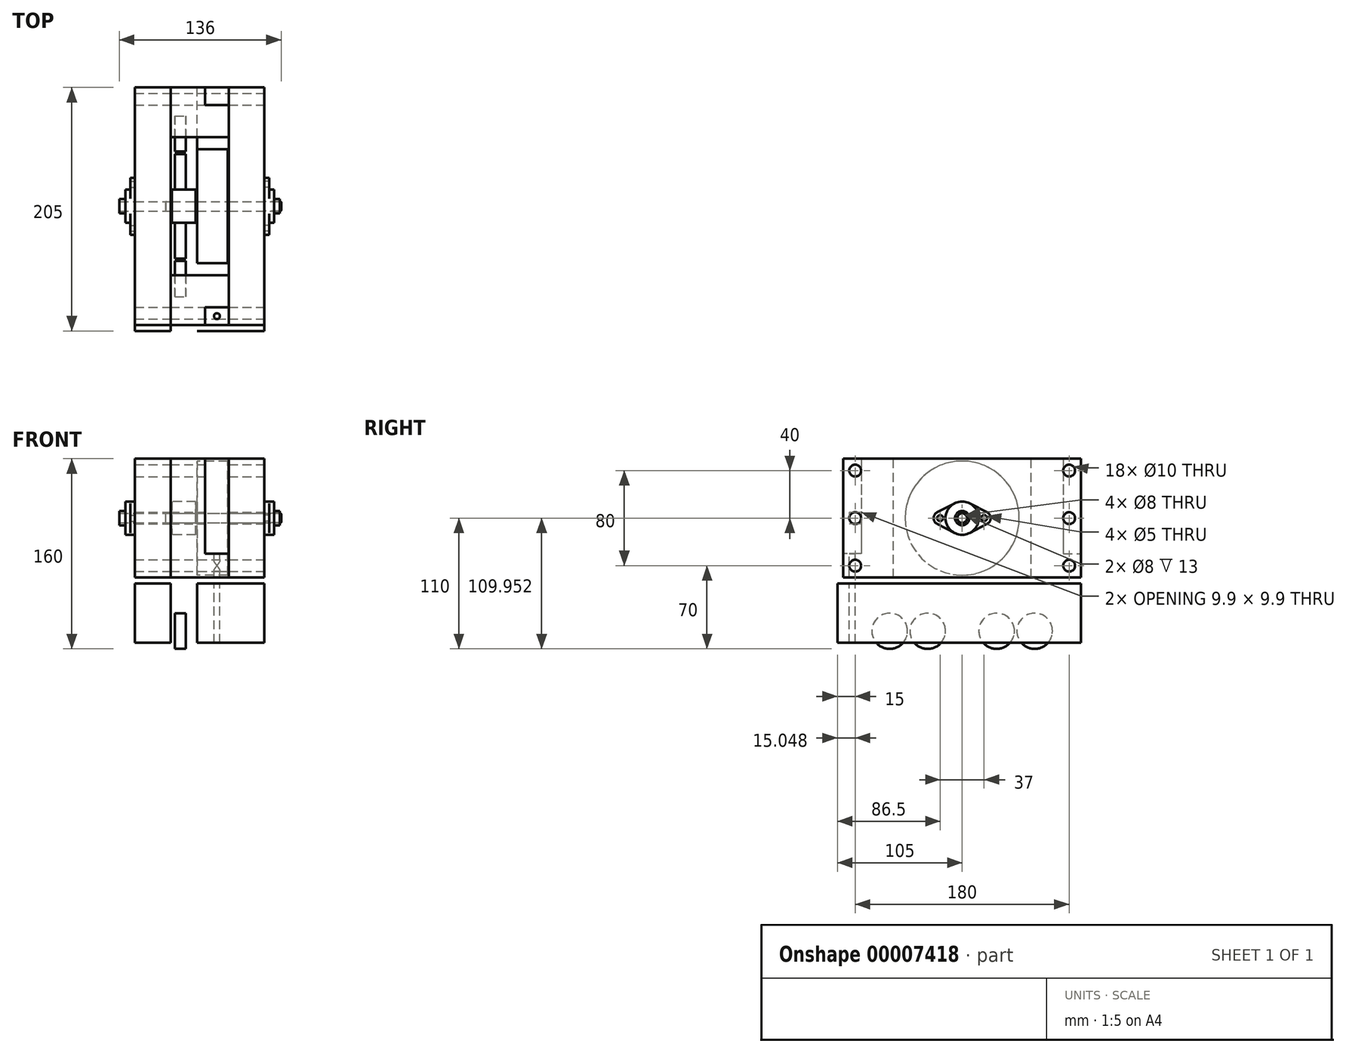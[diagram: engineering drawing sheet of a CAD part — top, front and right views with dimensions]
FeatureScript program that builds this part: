
annotation { "Feature Type Name" : "Feature", "Feature Type Description" : "" }
export const myFeature = defineFeature(function(context is Context, id is Id, definition is map)
    precondition{}
    {
        {
            var Q0;
            Q0=qCreatedBy(makeId("Front.planeOp"),FACE);
            var sketch = newSketch(context, id + "F0", { "sketchPlane" : qUnion([Q0])});
            skLineSegment(sketch, "E0.bottom", {"start": v(10, 14) * mm, "end": v(-10, 14) * mm});
            skLineSegment(sketch, "E0.top", {"start": v(10, -14) * mm, "end": v(4.5, -14) * mm});
            skLineSegment(sketch, "E0.left", {"start": v(10, 14) * mm, "end": v(10, -14) * mm});
            skLineSegment(sketch, "E0.right", {"start": v(-10, 14) * mm, "end": v(-10, -14) * mm});
            skPoint(sketch, "E0.middle", {"position": v(0, 0) * mm});
            skLineSegment(sketch, "E1", {"start": v(0, 0) * mm, "end": v(134.05, 0) * mm, "construction": true});
            skLineSegment(sketch, "E2", {"start": v(0, 0) * mm, "end": v(-79.2, 0) * mm, "construction": true});
            skLineSegment(sketch, "E3.bottom", {"start": v(-41, 15) * mm, "end": v(-56, 15) * mm});
            skLineSegment(sketch, "E3.top", {"start": v(-41, -15) * mm, "end": v(-56, -15) * mm});
            skLineSegment(sketch, "E3.left", {"start": v(-41, 15) * mm, "end": v(-41, -15) * mm});
            skLineSegment(sketch, "E3.right", {"start": v(-56, 15) * mm, "end": v(-56, -15) * mm});
            skPoint(sketch, "E3.middle", {"position": v(-48.5, 0) * mm});
            skLineSegment(sketch, "E4.bottom", {"start": v(37, 48) * mm, "end": v(21.5, 48) * mm});
            skLineSegment(sketch, "E4.top", {"start": v(37, -48) * mm, "end": v(11.5, -48) * mm});
            skLineSegment(sketch, "E4.left", {"start": v(37, 48) * mm, "end": v(37, -48) * mm});
            skLineSegment(sketch, "E4.right", {"start": v(11.5, 48) * mm, "end": v(11.5, -48) * mm});
            skPoint(sketch, "E4.middle", {"position": v(24.25, 0) * mm});
            skLineSegment(sketch, "E5.bottom", {"start": v(83, 15) * mm, "end": v(68, 15) * mm});
            skLineSegment(sketch, "E5.top", {"start": v(83, -15) * mm, "end": v(68, -15) * mm});
            skLineSegment(sketch, "E5.left", {"start": v(83, 15) * mm, "end": v(83, -15) * mm});
            skLineSegment(sketch, "E5.right", {"start": v(68, 15) * mm, "end": v(68, -15) * mm});
            skPoint(sketch, "E5.middle", {"position": v(75.5, 0) * mm});
            skLineSegment(sketch, "E6.bottom", {"start": v(13, 127.89) * mm, "end": v(43, 127.89) * mm});
            skLineSegment(sketch, "E6.top", {"start": v(13, 77.89) * mm, "end": v(43, 77.89) * mm});
            skLineSegment(sketch, "E6.left", {"start": v(13, 127.89) * mm, "end": v(13, 77.89) * mm});
            skLineSegment(sketch, "E6.right", {"start": v(43, 127.89) * mm, "end": v(43, 77.89) * mm});
            skLineSegment(sketch, "E7", {"start": v(43, 77.89) * mm, "end": v(53, 77.89) * mm});
            skLineSegment(sketch, "E8", {"start": v(53, 77.89) * mm, "end": v(53, 127.89) * mm});
            skLineSegment(sketch, "E9", {"start": v(53, 127.89) * mm, "end": v(43, 127.89) * mm});
            skLineSegment(sketch, "E10.bottom", {"start": v(68, 50) * mm, "end": v(38, 50) * mm});
            skLineSegment(sketch, "E10.top", {"start": v(68, -50) * mm, "end": v(38, -50) * mm});
            skLineSegment(sketch, "E10.left", {"start": v(68, 50) * mm, "end": v(68, -50) * mm});
            skLineSegment(sketch, "E10.right", {"start": v(38, 50) * mm, "end": v(38, -50) * mm});
            skPoint(sketch, "E10.middle", {"position": v(53, 0) * mm});
            skLineSegment(sketch, "E11.bottom", {"start": v(-11, 50) * mm, "end": v(-41, 50) * mm});
            skLineSegment(sketch, "E11.top", {"start": v(-11, -50) * mm, "end": v(-41, -50) * mm});
            skLineSegment(sketch, "E11.left", {"start": v(-11, 50) * mm, "end": v(-11, -50) * mm});
            skLineSegment(sketch, "E11.right", {"start": v(-41, 50) * mm, "end": v(-41, -50) * mm});
            skPoint(sketch, "E11.middle", {"position": v(-26, 0) * mm});
            skLineSegment(sketch, "E12.bottom", {"start": v(98, 150) * mm, "end": v(68, 150) * mm});
            skLineSegment(sketch, "E12.top", {"start": v(98, -150) * mm, "end": v(68, -150) * mm});
            skLineSegment(sketch, "E12.left", {"start": v(98, 150) * mm, "end": v(98, -150) * mm});
            skLineSegment(sketch, "E12.right", {"start": v(68, 150) * mm, "end": v(68, -150) * mm});
            skPoint(sketch, "E12.middle", {"position": v(83, 0) * mm});
            skLineSegment(sketch, "E13", {"start": v(53, 127.89) * mm, "end": v(68, 127.89) * mm, "construction": true});
            skLineSegment(sketch, "E14", {"start": v(53, 77.89) * mm, "end": v(68, 77.89) * mm, "construction": true});
            skLineSegment(sketch, "E15", {"start": v(21.5, 48) * mm, "end": v(21.5, -48) * mm, "construction": true});
            skLineSegment(sketch, "E16", {"start": v(21.5, 48) * mm, "end": v(11.5, 48) * mm});
            skLineSegment(sketch, "E17", {"start": v(48, 77.89) * mm, "end": v(48, 48) * mm, "construction": true});
            skPoint(sketch, "E18", {"position": v(29.25, 48) * mm});
            skLineSegment(sketch, "E19", {"start": v(37, 48) * mm, "end": v(37, 127.89) * mm, "construction": true});
            skLineSegment(sketch, "E20", {"start": v(43, 77.89) * mm, "end": v(43, 48) * mm, "construction": true});
            skLineSegment(sketch, "E21", {"start": v(53, 77.89) * mm, "end": v(53, 48) * mm, "construction": true});
            skCircle(sketch, "E22", {"center": v(35, 102.89) * mm, "radius": 8 * mm, "construction": true});
            skLineSegment(sketch, "E23", {"start": v(35, 102.89) * mm, "end": v(53, 102.89) * mm, "construction": true});
            skLineSegment(sketch, "E24.bottom", {"start": v(98, 127.89) * mm, "end": v(138, 127.89) * mm});
            skLineSegment(sketch, "E24.top", {"start": v(98, 77.89) * mm, "end": v(138, 77.89) * mm});
            skLineSegment(sketch, "E24.left", {"start": v(98, 127.89) * mm, "end": v(98, 77.89) * mm});
            skLineSegment(sketch, "E24.right", {"start": v(138, 127.89) * mm, "end": v(138, 77.89) * mm});
            skCircle(sketch, "E25", {"center": v(116, 102.89) * mm, "radius": 8 * mm, "construction": true});
            skLineSegment(sketch, "E26", {"start": v(116, 102.89) * mm, "end": v(98, 102.89) * mm, "construction": true});
            skLineSegment(sketch, "E27.bottom", {"start": v(-41, -55) * mm, "end": v(-11, -55) * mm});
            skLineSegment(sketch, "E27.top", {"start": v(-41, -105) * mm, "end": v(-11, -105) * mm});
            skLineSegment(sketch, "E27.left", {"start": v(-41, -55) * mm, "end": v(-41, -105) * mm});
            skLineSegment(sketch, "E27.right", {"start": v(-11, -55) * mm, "end": v(-11, -105) * mm});
            skLineSegment(sketch, "E28.bottom", {"start": v(11.5, -55) * mm, "end": v(68, -55) * mm});
            skLineSegment(sketch, "E28.top", {"start": v(11.5, -105) * mm, "end": v(68, -105) * mm});
            skLineSegment(sketch, "E28.left", {"start": v(11.5, -55) * mm, "end": v(11.5, -105) * mm});
            skLineSegment(sketch, "E28.right", {"start": v(68, -55) * mm, "end": v(68, -105) * mm});
            skLineSegment(sketch, "E29.bottom", {"start": v(1.75, -80) * mm, "end": v(-7.25, -80) * mm});
            skLineSegment(sketch, "E29.top", {"start": v(1.75, -110) * mm, "end": v(-7.25, -110) * mm});
            skLineSegment(sketch, "E29.left", {"start": v(1.75, -80) * mm, "end": v(1.75, -110) * mm});
            skLineSegment(sketch, "E29.right", {"start": v(-7.25, -80) * mm, "end": v(-7.25, -110) * mm});
            skPoint(sketch, "E29.middle", {"position": v(-2.75, -95) * mm});
            skLineSegment(sketch, "E30", {"start": v(4.5, 14) * mm, "end": v(4.5, -14) * mm, "construction": true});
            skLineSegment(sketch, "E31", {"start": v(4.5, -14) * mm, "end": v(-10, -14) * mm});
            skLineSegment(sketch, "E32", {"start": v(-2.75, -14) * mm, "end": v(-2.75, -95) * mm, "construction": true});
            skSolve(sketch);
        }
        {
            var Q0;
            Q0=qCreatedBy(makeId("Right.planeOp"),FACE);
            var sketch = newSketch(context, id + "F1", { "sketchPlane" : qUnion([Q0])});
            skPoint(sketch, "E33.0", {"position": v(0, 0) * mm});
            skCircle(sketch, "E34", {"center": v(0, 0) * mm, "radius": 14 * mm});
            skSolve(sketch);
        }
        {
            var Q0;
            Q0 = qSketchRegion(id + "F1", true);
            extrude(context, id + "F2", {"entities" : qUnion([Q0]), "endBound" : BoundingType.SYMMETRIC, "depth" : 20 * mm});
        }
        {
            var Q0;
            Q0=sQuery(id+"F0.wireOp",EDGE,"E4.right");
            var Q1;
            Q1=makeQuery(id+"F2.opExtrude","CAP_FACE",FACE,{"disambiguationData":[OSD([sQuery(id+"F1.wireOp",EDGE,"E34")])],"isStart":false});
            cPlane(context, id + "F3", {"entities" : qUnion([Q0, Q1]), "cplaneType" : CPlaneType.LINE_ANGLE, "offset" : 25 * mm, "angle" : 0 * degree, "width" : 150 * mm, "height" : 150 * mm});
        }
        {
            var Q0;
            Q0=qCreatedBy(id+"F3.planeOp",FACE);
            var sketch = newSketch(context, id + "F4", { "sketchPlane" : qUnion([Q0])});
            skPoint(sketch, "E35.0", {"position": v(0, 0) * mm});
            skCircle(sketch, "E36", {"center": v(0, 0) * mm, "radius": 48 * mm});
            skSolve(sketch);
        }
        {
            var Q0;
            Q0 = qSketchRegion(id + "F4", true);
            var Q1;
            Q1=sQuery(id+"F0.wireOp",VERTEX,"E4.left.start");
            extrude(context, id + "F5", {"entities" : qUnion([Q0]), "endBound" : BoundingType.UP_TO_VERTEX, "oppositeDirection" : true, "endBoundEntityVertex" : qUnion([Q1]), "depth" : 25 * mm});
        }
        {
            var Q0;
            {var subQ3=sQuery(id+"F0.wireOp",EDGE,"E10.bottom");Q0=makeQuery(id+"F0.imprint","IMPRINT",FACE,{"disambiguationData":[TD([[makeQuery(id+"F0.imprint","IMPRINT",EDGE,{"derivedFrom":subQ3}),1.0]])]});}
            extrude(context, id + "F6", {"entities" : qUnion([Q0]), "endBound" : BoundingType.SYMMETRIC, "depth" : 200 * mm});
        }
        {
            var Q0;
            {var subQ2=sQuery(id+"F0.wireOp",EDGE,"E11.bottom");Q0=makeQuery(id+"F0.imprint","IMPRINT",FACE,{"disambiguationData":[TD([[makeQuery(id+"F0.imprint","IMPRINT",EDGE,{"derivedFrom":subQ2}),1.0]])]});}
            extrude(context, id + "F7", {"entities" : qUnion([Q0]), "endBound" : BoundingType.SYMMETRIC, "depth" : 200 * mm});
        }
        {
            var Q0;
            Q0=makeQuery(id+"F6.opExtrude","SWEPT_FACE",FACE,{"disambiguationData":[OSD([sQuery(id+"F0.wireOp",EDGE,"E10.right")])]});
            var sketch = newSketch(context, id + "F8", { "sketchPlane" : qUnion([Q0])});
            skCircle(sketch, "E37.0", {"center": v(0, 0) * mm, "radius": 48 * mm, "construction": true});
            skLineSegment(sketch, "E38", {"start": v(48, 50) * mm, "end": v(48, -50) * mm, "construction": true});
            skLineSegment(sketch, "E39.bottom", {"start": v(100, 50) * mm, "end": v(58, 50) * mm});
            skLineSegment(sketch, "E39.top", {"start": v(100, -50) * mm, "end": v(58, -50) * mm});
            skLineSegment(sketch, "E39.left", {"start": v(100, 50) * mm, "end": v(100, -50) * mm});
            skLineSegment(sketch, "E39.right", {"start": v(58, 50) * mm, "end": v(58, -50) * mm});
            skLineSegment(sketch, "E40.bottom", {"start": v(-100, 50) * mm, "end": v(-58, 50) * mm});
            skLineSegment(sketch, "E40.top", {"start": v(-100, -50) * mm, "end": v(-58, -50) * mm});
            skLineSegment(sketch, "E40.left", {"start": v(-100, 50) * mm, "end": v(-100, -50) * mm});
            skLineSegment(sketch, "E40.right", {"start": v(-58, 50) * mm, "end": v(-58, -50) * mm});
            skSolve(sketch);
        }
        {
            var Q0;
            Q0=makeQuery(id+"F8.imprint","IMPRINT",FACE,{"disambiguationData":[TD([[makeQuery(id+"F8.imprint","IMPRINT",EDGE,{"derivedFrom":sQuery(id+"F8.wireOp",EDGE,"E39.bottom")}),1.0]])]});
            var Q1;
            Q1=makeQuery(id+"F7.opExtrude","SWEPT_FACE",FACE,{"disambiguationData":[OSD([sQuery(id+"F0.wireOp",EDGE,"E11.left")])]});
            extrude(context, id + "F9", {"entities" : qUnion([Q0]), "endBound" : BoundingType.UP_TO_SURFACE, "endBoundEntityFace" : qUnion([Q1]), "depth" : 25 * mm});
        }
        {
            var Q0;
            Q0=makeQuery(id+"F6.opExtrude","SWEPT_FACE",FACE,{"disambiguationData":[OSD([sQuery(id+"F0.wireOp",EDGE,"E12.right")])]});
            var Q1;
            Q1=makeQuery(id+"F7.opExtrude","SWEPT_FACE",FACE,{"disambiguationData":[OSD([sQuery(id+"F0.wireOp",EDGE,"E11.right")])]});
            cPlane(context, id + "F10", {"entities" : qUnion([Q0, Q1]), "cplaneType" : CPlaneType.MID_PLANE, "offset" : 25 * mm, "width" : 150 * mm, "height" : 150 * mm});
        }
        {
            var Q0;
            Q0=makeQuery(id+"F6.opExtrude","SWEPT_FACE",FACE,{"disambiguationData":[OSD([sQuery(id+"F0.wireOp",EDGE,"E12.right")])]});
            var sketch = newSketch(context, id + "F11", { "sketchPlane" : qUnion([Q0])});
            skCircle(sketch, "E41", {"center": v(0, 0) * mm, "radius": 4 * mm});
            skLineSegment(sketch, "E42", {"start": v(0, 0) * mm, "end": v(-18.5, 0) * mm, "construction": true});
            skCircle(sketch, "E43", {"center": v(-18.5, 0) * mm, "radius": 2.5 * mm});
            skLineSegment(sketch, "E44", {"start": v(0, 0) * mm, "end": v(0, 14) * mm, "construction": true});
            skLineSegment(sketch, "E45", {"start": v(-6.43, 12.43) * mm, "end": v(-21.03, 4.89) * mm});
            skLineSegment(sketch, "E46", {"start": v(-6.43, -12.43) * mm, "end": v(-21.03, -4.89) * mm});
            skLineSegment(sketch, "E47", {"start": v(-18.5, 0) * mm, "end": v(-30.47, 0) * mm, "construction": true});
            skPoint(sketch, "E48.visualSharp", {"position": v(-30.47, 0) * mm});
            skArc(sketch, "E48.filletArc", {"start": v(-21.03, 4.89) * mm, "mid": v(-24, 0) * mm, "end": v(-21.03, -4.89) * mm});
            skPoint(sketch, "E49", {"position": v(-24, 0) * mm});
            skPoint(sketch, "E49.positionSnap0", {"position": v(-24, 0) * mm});
            skLineSegment(sketch, "E50.MirrorCS", {"start": v(6.43, 12.43) * mm, "end": v(21.03, 4.89) * mm});
            skArc(sketch, "E51.MirrorCS", {"start": v(21.03, 4.89) * mm, "mid": v(24, 0) * mm, "end": v(21.03, -4.89) * mm});
            skLineSegment(sketch, "E52.MirrorCS", {"start": v(6.43, -12.43) * mm, "end": v(21.03, -4.89) * mm});
            skCircle(sketch, "E53.MirrorC", {"center": v(18.5, 0) * mm, "radius": 2.5 * mm});
            skArc(sketch, "E54", {"start": v(-6.43, 12.43) * mm, "mid": v(-14, 0) * mm, "end": v(-6.43, -12.43) * mm, "construction": true});
            skArc(sketch, "E55", {"start": v(-6.43, -12.43) * mm, "mid": v(0, -14) * mm, "end": v(6.43, -12.43) * mm});
            skArc(sketch, "E56", {"start": v(6.43, 12.43) * mm, "mid": v(0, 14) * mm, "end": v(-6.43, 12.43) * mm});
            skArc(sketch, "E57", {"start": v(6.43, -12.43) * mm, "mid": v(14, 0) * mm, "end": v(6.43, 12.43) * mm, "construction": true});
            skSolve(sketch);
        }
        {
            var Q0;
            Q0 = qSketchRegion(id + "F11", true);
            extrude(context, id + "F12", {"entities" : qUnion([Q0]), "depth" : 4 * mm});
        }
        {
            var Q0;
            Q0=makeQuery(id+"F12.opExtrude","CAP_FACE",FACE,{"disambiguationData":[OSD([sQuery(id+"F11.wireOp",EDGE,"E41"),sQuery(id+"F11.wireOp",EDGE,"E43"),sQuery(id+"F11.wireOp",EDGE,"E45"),sQuery(id+"F11.wireOp",EDGE,"E46"),sQuery(id+"F11.wireOp",EDGE,"E48.filletArc"),sQuery(id+"F11.wireOp",EDGE,"E50.MirrorCS"),sQuery(id+"F11.wireOp",EDGE,"E51.MirrorCS"),sQuery(id+"F11.wireOp",EDGE,"E52.MirrorCS"),sQuery(id+"F11.wireOp",EDGE,"E53.MirrorC"),sQuery(id+"F11.wireOp",EDGE,"E55"),sQuery(id+"F11.wireOp",EDGE,"E56")])],"isStart":false});
            var sketch = newSketch(context, id + "F13", { "sketchPlane" : qUnion([Q0])});
            skCircle(sketch, "E58", {"center": v(0, 0) * mm, "radius": 14 * mm});
            skCircle(sketch, "E59", {"center": v(0, 0) * mm, "radius": 4 * mm});
            skSolve(sketch);
        }
        {
            var Q0;
            Q0 = qSketchRegion(id + "F13", true);
            extrude(context, id + "F14", {"entities" : qUnion([Q0]), "operationType" : NewBodyOperationType.ADD, "depth" : 4 * mm});
        }
        {
            var Q0;
            Q0=makeQuery(id+"F14.opExtrude","CAP_FACE",FACE,{"disambiguationData":[OSD([sQuery(id+"F13.wireOp",EDGE,"E58"),sQuery(id+"F13.wireOp",EDGE,"E59")])],"isStart":false});
            var sketch = newSketch(context, id + "F15", { "sketchPlane" : qUnion([Q0])});
            skCircle(sketch, "E60.0", {"center": v(0, 0) * mm, "radius": 4 * mm});
            skCircle(sketch, "E61", {"center": v(0, 0) * mm, "radius": 6 * mm});
            skSolve(sketch);
        }
        {
            var Q0;
            Q0 = qSketchRegion(id + "F15", true);
            extrude(context, id + "F16", {"entities" : qUnion([Q0]), "operationType" : NewBodyOperationType.ADD, "depth" : 5 * mm});
        }
        {
            var Q0;
            Q0=makeQuery(id+"F12.opExtrude","SWEPT_BODY",BODY,{"disambiguationData":[OSD([sQuery(id+"F11.wireOp",EDGE,"E41"),sQuery(id+"F11.wireOp",EDGE,"E43"),sQuery(id+"F11.wireOp",EDGE,"E45"),sQuery(id+"F11.wireOp",EDGE,"E46"),sQuery(id+"F11.wireOp",EDGE,"E48.filletArc"),sQuery(id+"F11.wireOp",EDGE,"E50.MirrorCS"),sQuery(id+"F11.wireOp",EDGE,"E51.MirrorCS"),sQuery(id+"F11.wireOp",EDGE,"E52.MirrorCS"),sQuery(id+"F11.wireOp",EDGE,"E53.MirrorC"),sQuery(id+"F11.wireOp",EDGE,"E55"),sQuery(id+"F11.wireOp",EDGE,"E56")])]});
            var Q1;
            Q1=qCreatedBy(id+"F10.planeOp",FACE);
            mirror(context, id + "F17", {"entities" : qUnion([Q0]), "mirrorPlane" : qUnion([Q1])});
        }
        {
            var Q0;
            Q0=makeQuery(id+"F6.opExtrude","SWEPT_FACE",FACE,{"disambiguationData":[OSD([sQuery(id+"F0.wireOp",EDGE,"E12.right")])]});
            var sketch = newSketch(context, id + "F18", { "sketchPlane" : qUnion([Q0])});
            skCircle(sketch, "E62", {"center": v(0, 0) * mm, "radius": 4 * mm});
            skSolve(sketch);
        }
        {
            var Q0;
            Q0 = qSketchRegion(id + "F18", true);
            extrude(context, id + "F19", {"entities" : qUnion([Q0]), "operationType" : NewBodyOperationType.REMOVE, "endBound" : BoundingType.THROUGH_ALL, "oppositeDirection" : true, "depth" : 25 * mm});
        }
        {
            var Q0;
            Q0=makeQuery(id+"F0.imprint","IMPRINT",FACE,{"disambiguationData":[TD([[makeQuery(id+"F0.imprint","IMPRINT",EDGE,{"derivedFrom":sQuery(id+"F0.wireOp",EDGE,"E28.bottom")}),-1.0]])]});
            extrude(context, id + "F20", {"entities" : qUnion([Q0]), "endBound" : BoundingType.SYMMETRIC, "depth" : 200 * mm});
        }
        {
            var Q0;
            Q0=makeQuery(id+"F0.imprint","IMPRINT",FACE,{"disambiguationData":[TD([[makeQuery(id+"F0.imprint","IMPRINT",EDGE,{"derivedFrom":sQuery(id+"F0.wireOp",EDGE,"E27.bottom")}),-1.0]])]});
            extrude(context, id + "F21", {"entities" : qUnion([Q0]), "endBound" : BoundingType.SYMMETRIC, "depth" : 200 * mm});
        }
        {
            var Q0;
            Q0=sQuery(id+"F0.wireOp",EDGE,"E29.left");
            var Q1;
            Q1=makeQuery(id+"F20.opExtrude","SWEPT_FACE",FACE,{"disambiguationData":[OSD([sQuery(id+"F0.wireOp",EDGE,"E28.left")])]});
            cPlane(context, id + "F22", {"entities" : qUnion([Q0, Q1]), "cplaneType" : CPlaneType.LINE_ANGLE, "offset" : 25 * mm, "angle" : 0 * degree, "width" : 150 * mm, "height" : 150 * mm});
        }
        {
            var Q0;
            Q0=qCreatedBy(id+"F22.planeOp",FACE);
            var sketch = newSketch(context, id + "F23", { "sketchPlane" : qUnion([Q0])});
            skCircle(sketch, "E63.0", {"center": v(0, 0) * mm, "radius": 14 * mm, "construction": true});
            skLineSegment(sketch, "E64", {"start": v(0, 0) * mm, "end": v(0, -105) * mm, "construction": true});
            skPoint(sketch, "E65.0", {"position": v(0, -95) * mm});
            skLineSegment(sketch, "E66", {"start": v(0, -95) * mm, "end": v(-29, -95) * mm, "construction": true});
            skLineSegment(sketch, "E67", {"start": v(-29, -95) * mm, "end": v(-61, -95) * mm, "construction": true});
            skCircle(sketch, "E68", {"center": v(-29, -95) * mm, "radius": 15 * mm});
            skLineSegment(sketch, "E69", {"start": v(-14, 0) * mm, "end": v(-14, -95) * mm, "construction": true});
            skLineSegment(sketch, "E70", {"start": v(-14, 0) * mm, "end": v(0, 0) * mm, "construction": true});
            skCircle(sketch, "E71", {"center": v(-61, -95) * mm, "radius": 15 * mm});
            skPoint(sketch, "E72", {"position": v(-44, -95) * mm});
            skPoint(sketch, "E73", {"position": v(-46, -95) * mm});
            skCircle(sketch, "E74.MirrorC", {"center": v(29, -95) * mm, "radius": 15 * mm});
            skCircle(sketch, "E75.MirrorC", {"center": v(61, -95) * mm, "radius": 15 * mm});
            skSolve(sketch);
        }
        {
            var Q0;
            Q0 = qSketchRegion(id + "F23", true);
            extrude(context, id + "F24", {"entities" : qUnion([Q0]), "oppositeDirection" : true, "depth" : 9 * mm});
        }
        {
            var Q0;
            Q0=makeQuery(id+"F9.opExtrude","SWEPT_FACE",FACE,{"disambiguationData":[OSD([sQuery(id+"F8.wireOp",EDGE,"E39.left")])]});
            var sketch = newSketch(context, id + "F25", { "sketchPlane" : qUnion([Q0])});
            skLineSegment(sketch, "E76.bottom", {"start": v(38, 50) * mm, "end": v(18, 50) * mm});
            skLineSegment(sketch, "E76.top", {"start": v(38, -30) * mm, "end": v(18, -30) * mm});
            skLineSegment(sketch, "E76.left", {"start": v(38, 50) * mm, "end": v(38, -30) * mm});
            skLineSegment(sketch, "E76.right", {"start": v(18, 50) * mm, "end": v(18, -30) * mm});
            skSolve(sketch);
        }
        {
            var Q0;
            Q0=makeQuery(id+"F25.imprint","IMPRINT",FACE,{"disambiguationData":[TD([[makeQuery(id+"F25.imprint","IMPRINT",EDGE,{"derivedFrom":sQuery(id+"F25.wireOp",EDGE,"E76.bottom")}),-1.0]])]});
            extrude(context, id + "F26", {"entities" : qUnion([Q0]), "operationType" : NewBodyOperationType.REMOVE, "oppositeDirection" : true, "depth" : 15 * mm});
        }
        {
            var Q0;
            Q0=makeQuery(id+"F6.opExtrude","CAP_FACE",FACE,{"disambiguationData":[OSD([sQuery(id+"F0.wireOp",EDGE,"E10.bottom"),sQuery(id+"F0.wireOp",EDGE,"E10.top"),sQuery(id+"F0.wireOp",EDGE,"E10.right"),sQuery(id+"F0.wireOp",EDGE,"E12.right")])],"isStart":false});
            var Q1;
            Q1=makeQuery(id+"F6.opExtrude","CAP_FACE",FACE,{"disambiguationData":[OSD([sQuery(id+"F0.wireOp",EDGE,"E10.bottom"),sQuery(id+"F0.wireOp",EDGE,"E10.top"),sQuery(id+"F0.wireOp",EDGE,"E10.right"),sQuery(id+"F0.wireOp",EDGE,"E12.right")])],"isStart":true});
            cPlane(context, id + "F27", {"entities" : qUnion([Q0, Q1]), "cplaneType" : CPlaneType.MID_PLANE, "offset" : 25 * mm, "width" : 150 * mm, "height" : 150 * mm});
        }
        {
            var Q0;
            Q0=makeQuery(id+"F9.opExtrude","SWEPT_BODY",BODY,{"disambiguationData":[OSD([sQuery(id+"F8.wireOp",EDGE,"E39.bottom"),sQuery(id+"F8.wireOp",EDGE,"E39.top"),sQuery(id+"F8.wireOp",EDGE,"E39.left"),sQuery(id+"F8.wireOp",EDGE,"E39.right")])]});
            var Q1;
            Q1=qCreatedBy(id+"F27.planeOp",FACE);
            mirror(context, id + "F28", {"entities" : qUnion([Q0]), "mirrorPlane" : qUnion([Q1])});
        }
        {
            var Q0;
            Q0=makeQuery(id+"F26.boolean.opBoolean","COPY",FACE,{"derivedFrom":makeQuery(id+"F26.opExtrude","SWEPT_FACE",FACE,{"disambiguationData":[OSD([sQuery(id+"F25.wireOp",EDGE,"E76.top")])]})});
            var sketch = newSketch(context, id + "F29", { "sketchPlane" : qUnion([Q0])});
            skLineSegment(sketch, "E77", {"start": v(28, -85) * mm, "end": v(28, -92.5) * mm, "construction": true});
            skPoint(sketch, "E77.endSnap0", {"position": v(28, -85) * mm});
            skLineSegment(sketch, "E78", {"start": v(18, -92.5) * mm, "end": v(28, -92.5) * mm, "construction": true});
            skCircle(sketch, "E79", {"center": v(28, -92.5) * mm, "radius": 2.5 * mm});
            skSolve(sketch);
        }
        {
            var Q0;
            Q0 = qSketchRegion(id + "F29", true);
            extrude(context, id + "F30", {"entities" : qUnion([Q0]), "operationType" : NewBodyOperationType.REMOVE, "endBound" : BoundingType.THROUGH_ALL, "oppositeDirection" : true, "depth" : 25 * mm});
        }
        {
            var Q0;
            Q0=makeQuery(id+"F6.opExtrude","SWEPT_FACE",FACE,{"disambiguationData":[OSD([sQuery(id+"F0.wireOp",EDGE,"E12.right")])]});
            var sketch = newSketch(context, id + "F31", { "sketchPlane" : qUnion([Q0])});
            skLineSegment(sketch, "E80", {"start": v(-90, 50) * mm, "end": v(-90, 40) * mm, "construction": true});
            skLineSegment(sketch, "E81", {"start": v(-90, 40) * mm, "end": v(-90, 0) * mm, "construction": true});
            skLineSegment(sketch, "E82", {"start": v(-90, 0) * mm, "end": v(-90, -40) * mm, "construction": true});
            skLineSegment(sketch, "E83", {"start": v(-90, -40) * mm, "end": v(-90, -50) * mm, "construction": true});
            skCircle(sketch, "E84", {"center": v(-90, 40) * mm, "radius": 5 * mm});
            skCircle(sketch, "E85", {"center": v(-90, 0) * mm, "radius": 5 * mm});
            skCircle(sketch, "E86", {"center": v(-90, -40) * mm, "radius": 5 * mm});
            skLineSegment(sketch, "E87", {"start": v(0, 50) * mm, "end": v(0, -50) * mm, "construction": true});
            skCircle(sketch, "E88.MirrorC", {"center": v(90, 40) * mm, "radius": 5 * mm});
            skCircle(sketch, "E89.MirrorC", {"center": v(90, 0) * mm, "radius": 5 * mm});
            skCircle(sketch, "E90.MirrorC", {"center": v(90, -40) * mm, "radius": 5 * mm});
            skSolve(sketch);
        }
        {
            var Q0;
            Q0 = qSketchRegion(id + "F31", true);
            extrude(context, id + "F32", {"entities" : qUnion([Q0]), "operationType" : NewBodyOperationType.REMOVE, "endBound" : BoundingType.THROUGH_ALL, "oppositeDirection" : true, "depth" : 25 * mm});
        }
        {
            var Q0;
            Q0=makeQuery(id+"F16.opExtrude","CAP_FACE",FACE,{"disambiguationData":[OSD([sQuery(id+"F15.wireOp",EDGE,"E60.0"),sQuery(id+"F15.wireOp",EDGE,"E61")])],"isStart":false});
            var sketch = newSketch(context, id + "F33", { "sketchPlane" : qUnion([Q0])});
            skCircle(sketch, "E91.0", {"center": v(0, 0) * mm, "radius": 4 * mm});
            skSolve(sketch);
        }
        {
            var Q0;
            Q0 = qSketchRegion(id + "F33", true);
            extrude(context, id + "F34", {"entities" : qUnion([Q0]), "oppositeDirection" : true, "depth" : 96 * mm, "hasSecondDirection" : true, "secondDirectionOppositeDirection" : false, "secondDirectionDepth" : 1 * mm});
        }
        {
            var Q0;
            Q0=makeQuery(id+"F34.opExtrude","CAP_EDGE",EDGE,{"disambiguationData":[OSD([sQuery(id+"F33.wireOp",EDGE,"E91.0")])],"isStart":true});
            var Q1;
            Q1=makeQuery(id+"F34.opExtrude","CAP_EDGE",EDGE,{"disambiguationData":[OSD([sQuery(id+"F33.wireOp",EDGE,"E91.0")])],"isStart":false});
            fillet(context, id + "F35", {"entities" : qUnion([Q0, Q1]), "radius" : 0.5 * mm, "tangentPropagation" : true, "conicFillet" : false});
        }
        {
            var Q0;
            Q0=makeQuery(id+"F20.opExtrude","CAP_FACE",FACE,{"disambiguationData":[OSD([sQuery(id+"F0.wireOp",EDGE,"E28.bottom"),sQuery(id+"F0.wireOp",EDGE,"E28.top"),sQuery(id+"F0.wireOp",EDGE,"E28.left"),sQuery(id+"F0.wireOp",EDGE,"E28.right")])],"isStart":false});
            var Q1;
            Q1=makeQuery(id+"F21.opExtrude","CAP_FACE",FACE,{"disambiguationData":[OSD([sQuery(id+"F0.wireOp",EDGE,"E27.bottom"),sQuery(id+"F0.wireOp",EDGE,"E27.top"),sQuery(id+"F0.wireOp",EDGE,"E27.left"),sQuery(id+"F0.wireOp",EDGE,"E27.right")])],"isStart":false});
            extrude(context, id + "F36", {"entities" : qUnion([Q0, Q1]), "operationType" : NewBodyOperationType.ADD, "depth" : 5 * mm});
        }
    });
